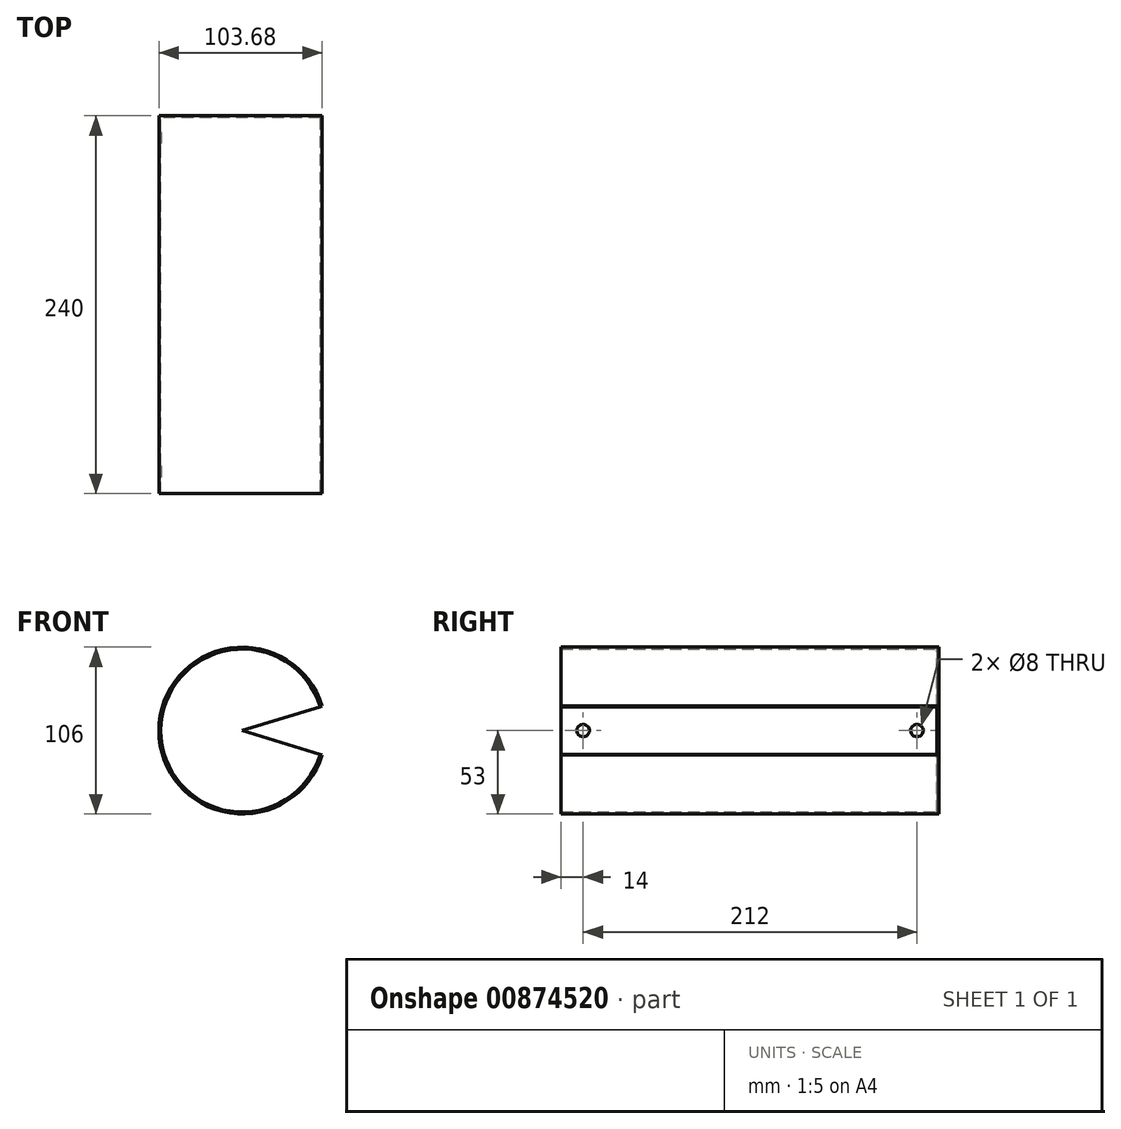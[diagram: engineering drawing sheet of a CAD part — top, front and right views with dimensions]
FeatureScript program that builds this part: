
annotation { "Feature Type Name" : "Feature", "Feature Type Description" : "" }
export const myFeature = defineFeature(function(context is Context, id is Id, definition is map)
    precondition{}
    {
        {
            var Q0;
            Q0=qCreatedBy(makeId("Front.planeOp"),FACE);
            var sketch = newSketch(context, id + "F0", { "sketchPlane" : qUnion([Q0])});
            skCircle(sketch, "E0", {"center": v(0, 0) * mm, "radius": 53 * mm});
            skSolve(sketch);
        }
        {
            var Q0;
            Q0 = qSketchRegion(id + "F0", true);
            extrude(context, id + "F1", {"entities" : qUnion([Q0]), "depth" : 240 * mm, "offsetDistance" : 25 * mm});
        }
        {
            var Q0;
            Q0=makeQuery(id+"F1.opExtrude","CAP_FACE",FACE,{"disambiguationData":[OSD([sQuery(id+"F0.wireOp",EDGE,"E0")])],"isStart":false});
            var sketch = newSketch(context, id + "F2", { "sketchPlane" : qUnion([Q0])});
            skLineSegment(sketch, "E1", {"start": v(0, 0) * mm, "end": v(50.68, 0) * mm});
            skLineSegment(sketch, "E2", {"start": v(50.68, 0) * mm, "end": v(50.68, -15.5) * mm});
            skLineSegment(sketch, "E3", {"start": v(50.68, -15.5) * mm, "end": v(50.68, 15.5) * mm});
            skArc(sketch, "E4", {"start": v(50.68, -15.5) * mm, "mid": v(57.12, 0) * mm, "end": v(50.68, 15.5) * mm});
            skSolve(sketch);
        }
        {
            var Q0;
            {var subQ0=sQuery(id+"F2.wireOp",EDGE,"E4");Q0=makeQuery(id+"F2.imprint","IMPRINT",FACE,{"disambiguationData":[TD([[makeQuery(id+"F2.imprint","IMPRINT",EDGE,{"derivedFrom":subQ0}),1.0]])]});}
            var Q1;
            {var subQ0=sQuery(id+"F2.wireOp",EDGE,"E3");var subQ1=makeQuery(id+"F2.imprint","IMPRINT",VERTEX,{"derivedFrom":subQ0});Q1=makeQuery(id+"F2.imprint","IMPRINT",FACE,{"disambiguationData":[TD([[makeQuery(id+"F2.imprint","IMPRINT",EDGE,{"disambiguationData":[TD([[subQ1,1.0]])],"derivedFrom":subQ0}),-1.0]])]});}
            extrude(context, id + "F3", {"entities" : qUnion([Q0, Q1]), "operationType" : NewBodyOperationType.REMOVE, "oppositeDirection" : true, "depth" : 240 * mm, "offsetDistance" : 25 * mm});
        }
        {
            var Q0;
            Q0=makeQuery(id+"F1.opExtrude","CAP_FACE",FACE,{"disambiguationData":[OSD([sQuery(id+"F0.wireOp",EDGE,"E0")])],"isStart":false});
            shell(context, id + "F4", {"entities" : qUnion([Q0]), "thickness" : 1.25 * mm});
        }
        {
            var Q0;
            Q0=makeQuery(id+"F1.opExtrude","CAP_FACE",FACE,{"disambiguationData":[OSD([sQuery(id+"F0.wireOp",EDGE,"E0")])],"isStart":true});
            var sketch = newSketch(context, id + "F5", { "sketchPlane" : qUnion([Q0])});
            skCircle(sketch, "E5", {"center": v(0, 0) * mm, "radius": 53 * mm});
            skCircle(sketch, "E6", {"center": v(0, 0) * mm, "radius": 51.75 * mm});
            skLineSegment(sketch, "E7", {"start": v(0, 0) * mm, "end": v(-50.68, 15.5) * mm});
            skLineSegment(sketch, "E8", {"start": v(-50.68, 15.5) * mm, "end": v(0, 0) * mm});
            skLineSegment(sketch, "E9", {"start": v(0, 0) * mm, "end": v(-50.68, -15.5) * mm});
            skSolve(sketch);
        }
        {
            var Q0;
            {var subQ0=sQuery(id+"F5.wireOp",EDGE,"E8");var subQ1=sQuery(id+"F5.wireOp",EDGE,"E6");var subQ2=makeQuery(id+"F5.imprint","INTERSECT",VERTEX,{"derivedFrom":[subQ1,subQ0]});Q0=makeQuery(id+"F5.imprint","IMPRINT",FACE,{"disambiguationData":[TD([[makeQuery(id+"F5.imprint","IMPRINT",EDGE,{"disambiguationData":[TD([[subQ2,1.0]])],"derivedFrom":subQ1}),1.0]])]});}
            var Q1;
            {var subQ1=sQuery(id+"F5.wireOp",EDGE,"E8");var subQ3=sQuery(id+"F5.wireOp",EDGE,"E6");var subQ7=makeQuery(id+"F5.imprint","INTERSECT",VERTEX,{"derivedFrom":[subQ3,subQ1]});Q1=makeQuery(id+"F5.imprint","IMPRINT",FACE,{"disambiguationData":[TD([[makeQuery(id+"F5.imprint","IMPRINT",EDGE,{"disambiguationData":[TD([[subQ7,-1.0]])],"derivedFrom":subQ3}),1.0]])]});}
            var Q2;
            {var subQ0=sQuery(id+"F5.wireOp",EDGE,"E9");var subQ1=sQuery(id+"F5.wireOp",EDGE,"E6");var subQ2=makeQuery(id+"F5.imprint","INTERSECT",VERTEX,{"derivedFrom":[subQ1,subQ0]});Q2=makeQuery(id+"F5.imprint","IMPRINT",FACE,{"disambiguationData":[TD([[makeQuery(id+"F5.imprint","IMPRINT",EDGE,{"disambiguationData":[TD([[subQ2,1.0]])],"derivedFrom":subQ1}),-1.0]])]});}
            var Q3;
            {var subQ0=sQuery(id+"F5.wireOp",EDGE,"E8");var subQ1=sQuery(id+"F5.wireOp",EDGE,"E6");var subQ2=makeQuery(id+"F5.imprint","INTERSECT",VERTEX,{"derivedFrom":[subQ1,subQ0]});Q3=makeQuery(id+"F5.imprint","IMPRINT",FACE,{"disambiguationData":[TD([[makeQuery(id+"F5.imprint","IMPRINT",EDGE,{"disambiguationData":[TD([[subQ2,-1.0]])],"derivedFrom":subQ1}),-1.0]])]});}
            extrude(context, id + "F6", {"entities" : qUnion([Q0, Q1, Q2, Q3]), "operationType" : NewBodyOperationType.REMOVE, "oppositeDirection" : true, "depth" : 260 * mm, "offsetDistance" : 25 * mm});
        }
        {
            var Q0;
            Q0=qCreatedBy(makeId("Right.planeOp"),FACE);
            var sketch = newSketch(context, id + "F7", { "sketchPlane" : qUnion([Q0])});
            skCircle(sketch, "E10", {"center": v(-14, 0) * mm, "radius": 4 * mm});
            skCircle(sketch, "E11", {"center": v(-226, 0) * mm, "radius": 4 * mm});
            skSolve(sketch);
        }
        {
            var Q0;
            Q0 = qSketchRegion(id + "F7", true);
            extrude(context, id + "F8", {"entities" : qUnion([Q0]), "operationType" : NewBodyOperationType.REMOVE, "oppositeDirection" : true, "depth" : 110 * mm, "offsetDistance" : 25 * mm});
        }
    });
